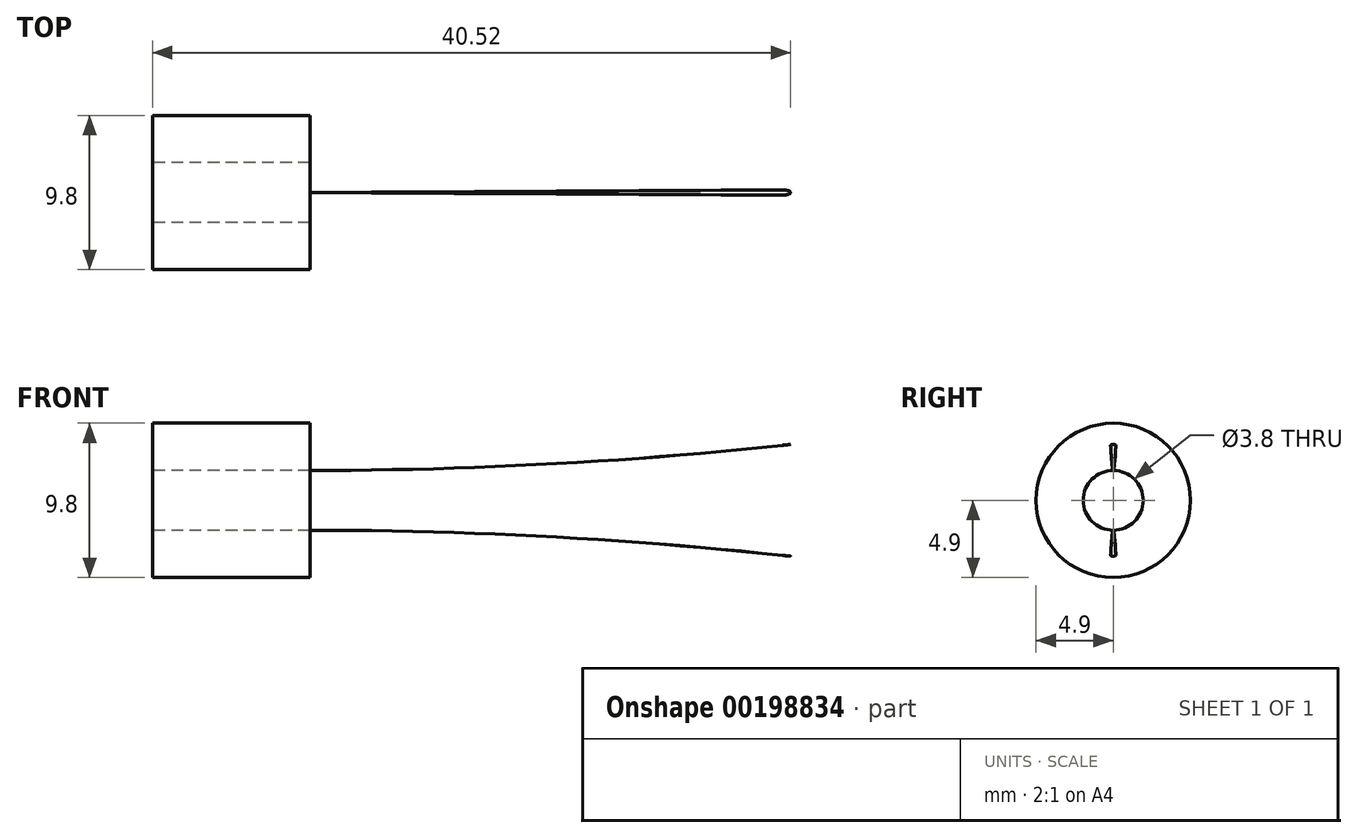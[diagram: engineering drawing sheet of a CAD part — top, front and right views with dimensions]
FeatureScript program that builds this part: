
annotation { "Feature Type Name" : "Feature", "Feature Type Description" : "" }
export const myFeature = defineFeature(function(context is Context, id is Id, definition is map)
    precondition{}
    {
        {
            var Q0;
            Q0=qCreatedBy(makeId("Front.planeOp"),FACE);
            var sketch = newSketch(context, id + "F0", { "sketchPlane" : qUnion([Q0])});
            skLineSegment(sketch, "E0.bottom", {"start": v(-25, 5) * mm, "end": v(0, 5) * mm, "construction": true});
            skLineSegment(sketch, "E0.top", {"start": v(-25, 3) * mm, "end": v(0, 3) * mm, "construction": true});
            skLineSegment(sketch, "E0.left", {"start": v(-25, 5) * mm, "end": v(-25, 3) * mm, "construction": true});
            skLineSegment(sketch, "E0.right", {"start": v(0, 5) * mm, "end": v(0, 3) * mm, "construction": true});
            skLineSegment(sketch, "E1", {"start": v(0, 2) * mm, "end": v(41.13, 2) * mm, "construction": true});
            skLineSegment(sketch, "E2", {"start": v(0, 1.9) * mm, "end": v(2.44, 1.9) * mm, "construction": true});
            skArc(sketch, "E3", {"start": v(0, 1.9) * mm, "mid": v(15.02, 2.3) * mm, "end": v(30, 3.5) * mm});
            skLineSegment(sketch, "E4", {"start": v(30, 32.1) * mm, "end": v(30, 2) * mm, "construction": true});
            skLineSegment(sketch, "E5", {"start": v(40, 32.1) * mm, "end": v(40, 2) * mm, "construction": true});
            skLineSegment(sketch, "E6", {"start": v(0, 1.9) * mm, "end": v(-10, 1.9) * mm});
            skArc(sketch, "E7", {"start": v(0, 0.5) * mm, "mid": v(21.56, 1.32) * mm, "end": v(43, 3.78) * mm});
            skLineSegment(sketch, "E8", {"start": v(43, 32.1) * mm, "end": v(43, 2) * mm, "construction": true});
            skLineSegment(sketch, "E9", {"start": v(38.89, 1.75) * mm, "end": v(41.13, 1.75) * mm, "construction": true});
            skArc(sketch, "E10", {"start": v(30, 3.5) * mm, "mid": v(35.12, 3.33) * mm, "end": v(40, 1.75) * mm});
            skLineSegment(sketch, "E11", {"start": v(-26.97, 0) * mm, "end": v(16.55, 0) * mm, "construction": true});
            skArc(sketch, "E12", {"start": v(0, 0.5) * mm, "mid": v(-5.05, 0.85) * mm, "end": v(-10, 1.9) * mm});
            skSolve(sketch);
        }
        {
            var Q0;
            Q0=qCreatedBy(makeId("Right.planeOp"),FACE);
            var Q1;
            Q1=sQuery(id+"F0.wireOp",VERTEX,"E6.end");
            cPlane(context, id + "F1", {"entities" : qUnion([Q0, Q1]), "cplaneType" : CPlaneType.PLANE_POINT, "offset" : 25 * mm, "width" : 150 * mm, "height" : 150 * mm});
        }
        {
            var Q0;
            Q0=qCreatedBy(id+"F1.planeOp",FACE);
            var sketch = newSketch(context, id + "F2", { "sketchPlane" : qUnion([Q0])});
            skArc(sketch, "E13", {"start": v(1.9, 0) * mm, "mid": v(0, 1.9) * mm, "end": v(-1.9, 0) * mm});
            skLineSegment(sketch, "E14", {"start": v(-1.9, 0) * mm, "end": v(1.9, 0) * mm});
            skSolve(sketch);
        }
        {
            var Q0;
            Q0=makeQuery(id+"F2.imprint","IMPRINT",FACE,{"disambiguationData":[TD([[makeQuery(id+"F2.imprint","IMPRINT",EDGE,{"derivedFrom":sQuery(id+"F2.wireOp",EDGE,"E13")}),1.0]])]});
            var Q1;
            Q1=sQuery(id+"F0.wireOp",EDGE,"E6");
            var Q2;
            Q2=sQuery(id+"F0.wireOp",EDGE,"E3");
            var Q3;
            Q3=sQuery(id+"F0.wireOp",EDGE,"E10");
            sweep(context, id + "F3", {"profiles" : qUnion([Q0]), "path" : qUnion([Q1, Q2, Q3])});
        }
        {
            var Q0;
            Q0=qCreatedBy(makeId("Right.planeOp"),FACE);
            var Q1;
            Q1=sQuery(id+"F0.wireOp",VERTEX,"E12.end");
            cPlane(context, id + "F4", {"entities" : qUnion([Q0, Q1]), "cplaneType" : CPlaneType.PLANE_POINT, "offset" : 25 * mm, "width" : 150 * mm, "height" : 150 * mm});
        }
        {
            var Q0;
            Q0=qCreatedBy(id+"F4.planeOp",FACE);
            var sketch = newSketch(context, id + "F5", { "sketchPlane" : qUnion([Q0])});
            skLineSegment(sketch, "E15.bottom", {"start": v(-4.9, 1.9) * mm, "end": v(4.9, 1.9) * mm});
            skLineSegment(sketch, "E15.top", {"start": v(-4.9, -6) * mm, "end": v(4.9, -6) * mm});
            skLineSegment(sketch, "E15.left", {"start": v(-4.9, 1.9) * mm, "end": v(-4.9, -6) * mm});
            skLineSegment(sketch, "E15.right", {"start": v(4.9, 1.9) * mm, "end": v(4.9, -6) * mm});
            skPoint(sketch, "E16", {"position": v(0, 1.9) * mm});
            skSolve(sketch);
        }
        {
            var Q0;
            Q0=makeQuery(id+"F5.imprint","IMPRINT",FACE,{"disambiguationData":[TD([[makeQuery(id+"F5.imprint","IMPRINT",EDGE,{"derivedFrom":sQuery(id+"F5.wireOp",EDGE,"E15.bottom")}),-1.0]])]});
            var Q1;
            Q1=sQuery(id+"F0.wireOp",EDGE,"E12");
            var Q2;
            Q2=sQuery(id+"F0.wireOp",EDGE,"E7");
            sweep(context, id + "F6", {"operationType" : NewBodyOperationType.REMOVE, "profiles" : qUnion([Q0]), "path" : qUnion([Q1, Q2]), "keepProfileOrientation" : true});
        }
        {
            var Q0;
            Q0=makeQuery(id+"F3.opSweep","SWEPT_BODY",BODY,{"disambiguationData":[OSD([sQuery(id+"F0.wireOp",EDGE,"E10"),sQuery(id+"F2.wireOp",EDGE,"E13"),sQuery(id+"F2.wireOp",EDGE,"E14")])]});
            var Q1;
            Q1=qCreatedBy(makeId("Top.planeOp"),FACE);
            mirror(context, id + "F7", {"entities" : qUnion([Q0]), "mirrorPlane" : qUnion([Q1])});
        }
        {
            var Q0;
            Q0=qCreatedBy(makeId("Front.planeOp"),FACE);
            var sketch = newSketch(context, id + "F8", { "sketchPlane" : qUnion([Q0])});
            skLineSegment(sketch, "E17.bottom", {"start": v(-10, 4.9) * mm, "end": v(0, 4.9) * mm});
            skLineSegment(sketch, "E17.top", {"start": v(-10, 1.9) * mm, "end": v(0, 1.9) * mm});
            skLineSegment(sketch, "E17.left", {"start": v(-10, 4.9) * mm, "end": v(-10, 1.9) * mm});
            skLineSegment(sketch, "E17.right", {"start": v(0, 4.9) * mm, "end": v(0, 1.9) * mm});
            skSolve(sketch);
        }
        {
            var Q0;
            Q0=makeQuery(id+"F8.imprint","IMPRINT",FACE,{"disambiguationData":[TD([[makeQuery(id+"F8.imprint","IMPRINT",EDGE,{"derivedFrom":sQuery(id+"F8.wireOp",EDGE,"E17.bottom")}),-1.0]])]});
            var Q1;
            Q1=sQuery(id+"F0.wireOp",EDGE,"E11");
            revolve(context, id + "F9", {"entities" : qUnion([Q0]), "axis" : qUnion([Q1]), "revolveType" : RevolveType.FULL});
        }
    });
